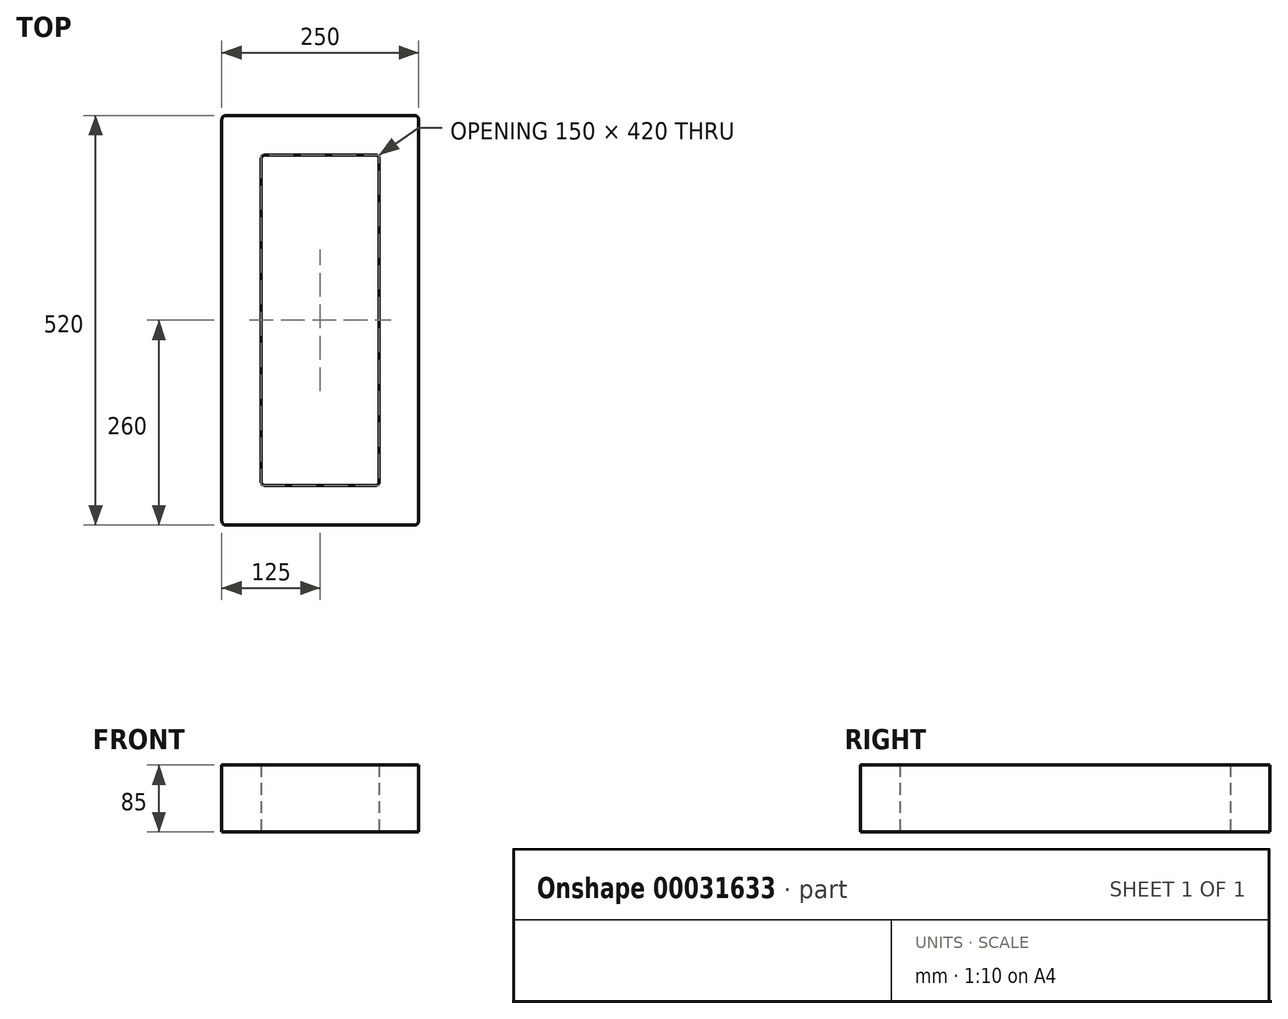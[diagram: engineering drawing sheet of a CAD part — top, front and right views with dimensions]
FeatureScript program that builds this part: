
annotation { "Feature Type Name" : "Feature", "Feature Type Description" : "" }
export const myFeature = defineFeature(function(context is Context, id is Id, definition is map)
    precondition{}
    {
        {
            var Q0;
            Q0=qCreatedBy(makeId("Top.planeOp"),FACE);
            var sketch = newSketch(context, id + "F0", { "sketchPlane" : qUnion([Q0])});
            skLineSegment(sketch, "E0.rect.bottom", {"start": v(-70, 210) * mm, "end": v(70, 210) * mm});
            skLineSegment(sketch, "E0.rect.top", {"start": v(-70, -210) * mm, "end": v(70, -210) * mm});
            skLineSegment(sketch, "E0.rect.left", {"start": v(-75, 205) * mm, "end": v(-75, -205) * mm});
            skLineSegment(sketch, "E0.rect.right", {"start": v(75, 205) * mm, "end": v(75, -205) * mm});
            skPoint(sketch, "E0.rect.middle", {"position": v(0, 0) * mm});
            skLineSegment(sketch, "E1.rect.bottom", {"start": v(-120, 260) * mm, "end": v(120, 260) * mm});
            skLineSegment(sketch, "E1.rect.top", {"start": v(-120, -260) * mm, "end": v(120, -260) * mm});
            skLineSegment(sketch, "E1.rect.left", {"start": v(-125, 255) * mm, "end": v(-125, -255) * mm});
            skLineSegment(sketch, "E1.rect.right", {"start": v(125, 255) * mm, "end": v(125, -255) * mm});
            skPoint(sketch, "E2.visualSharp", {"position": v(-125, 260) * mm});
            skArc(sketch, "E2.filletArc", {"start": v(-120, 260) * mm, "mid": v(-123.54, 258.54) * mm, "end": v(-125, 255) * mm});
            skPoint(sketch, "E3.visualSharp", {"position": v(125, 260) * mm});
            skArc(sketch, "E3.filletArc", {"start": v(125, 255) * mm, "mid": v(123.54, 258.54) * mm, "end": v(120, 260) * mm});
            skPoint(sketch, "E4.visualSharp", {"position": v(125, -260) * mm});
            skArc(sketch, "E4.filletArc", {"start": v(120, -260) * mm, "mid": v(123.54, -258.54) * mm, "end": v(125, -255) * mm});
            skPoint(sketch, "E5.visualSharp", {"position": v(-125, -260) * mm});
            skArc(sketch, "E5.filletArc", {"start": v(-125, -255) * mm, "mid": v(-123.54, -258.54) * mm, "end": v(-120, -260) * mm});
            skPoint(sketch, "E6.visualSharp", {"position": v(-75, -210) * mm});
            skArc(sketch, "E6.filletArc", {"start": v(-75, -205) * mm, "mid": v(-73.54, -208.54) * mm, "end": v(-70, -210) * mm});
            skPoint(sketch, "E7.visualSharp", {"position": v(75, -210) * mm});
            skArc(sketch, "E7.filletArc", {"start": v(70, -210) * mm, "mid": v(73.54, -208.54) * mm, "end": v(75, -205) * mm});
            skPoint(sketch, "E8.visualSharp", {"position": v(75, 210) * mm});
            skArc(sketch, "E8.filletArc", {"start": v(75, 205) * mm, "mid": v(73.54, 208.54) * mm, "end": v(70, 210) * mm});
            skPoint(sketch, "E9.visualSharp", {"position": v(-75, 210) * mm});
            skArc(sketch, "E9.filletArc", {"start": v(-70, 210) * mm, "mid": v(-73.54, 208.54) * mm, "end": v(-75, 205) * mm});
            skSolve(sketch);
        }
        {
            var Q0;
            Q0=makeQuery(id+"F0.imprint","IMPRINT",FACE,{"disambiguationData":[TD([[makeQuery(id+"F0.imprint","IMPRINT",EDGE,{"derivedFrom":sQuery(id+"F0.wireOp",EDGE,"E0.rect.bottom")}),1.0]])]});
            extrude(context, id + "F1", {"entities" : qUnion([Q0]), "depth" : 85 * mm});
        }
    });
